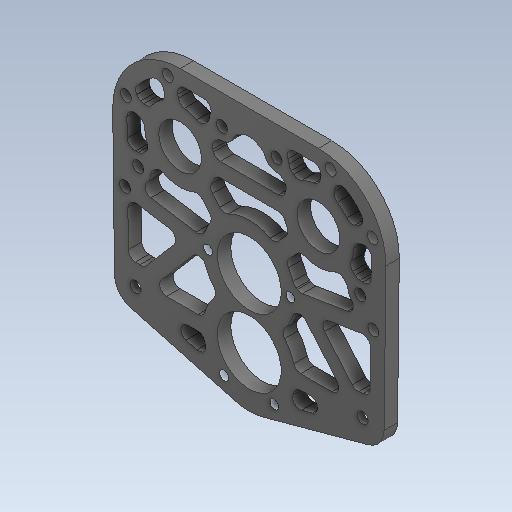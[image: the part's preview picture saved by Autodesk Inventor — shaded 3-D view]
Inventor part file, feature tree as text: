
AUTODESK INVENTOR PART (.ipt)
format: ipt  version: 2020 (Build 240168000, 168)  size: 384,000 bytes
history: native  units: in
note: dims shown in document units (in); Inventor stores cm internally (conversion verified against a paired STEP export)
features: fillet x1
ambient origin geometry x8: Origin, YZ Plane, XZ Plane, XY Plane, X Axis, Y Axis, Z Axis, Center Point
bodies: Solid1 (feature_tree)
feature tree (1):
  fillet  "Fillet2"  [1 undecoded]
note: 1 required parameter value undecoded (feature->parameter linkage not recoverable at this tier; creation-order binding heuristic only, values carry confidence <= 0.55)
